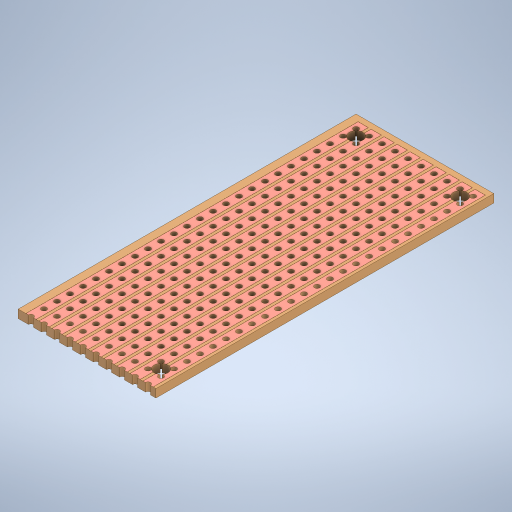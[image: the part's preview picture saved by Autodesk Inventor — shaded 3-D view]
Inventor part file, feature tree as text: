
AUTODESK INVENTOR PART (.ipt)
format: ipt  version: 2023 (Build 270158000, 158)  size: 1,360,384 bytes
history: mixed  units: in
note: dims shown in document units (in); Inventor stores cm internally (conversion verified against a paired STEP export)
features: sketch x10, extrude x9, projected_geometry x5, other x2, boolean_combine x1, imported_body x1
ambient origin geometry x8: Origin, YZ Plane, XZ Plane, XY Plane, X Axis, Y Axis, Z Axis, Center Point
bodies: Solid1 (imported_parasolid), Solid2 (imported_parasolid), Solid3 (imported_parasolid), Solid4 (imported_parasolid), Solid5 (imported_parasolid), Solid6 (imported_parasolid), Solid7 (imported_parasolid), Solid8 (imported_parasolid), Solid9 (imported_parasolid), Solid10 (imported_parasolid), Solid11 (imported_parasolid), Solid12 (imported_parasolid), Solid13 (imported_parasolid), Solid14 (imported_parasolid), Solid15 (imported_parasolid), Solid16 (imported_parasolid), Solid17 (imported_parasolid), Solid18 (imported_parasolid), Solid19 (imported_parasolid), Solid20 (imported_parasolid), Body2 (imported_parasolid), Body1 (imported_parasolid), Body3 (imported_parasolid), Body4 (imported_parasolid), Body5 (imported_parasolid), Body6 (imported_parasolid), Body7 (imported_parasolid), Body8 (imported_parasolid), Body9 (imported_parasolid), Body10 (imported_parasolid), Body11 (imported_parasolid), Body12 (imported_parasolid), Body13 (imported_parasolid), Body14 (imported_parasolid), Body15 (imported_parasolid), Body16 (imported_parasolid), Body17 (imported_parasolid), Body18 (imported_parasolid), Body19 (imported_parasolid), Body20 (imported_parasolid)
feature tree (28):
  other  "Repaired Geometry1"
  other  "Repaired Geometry2"
  sketch  "Sketch1"  dims[d0=0.1969in d1=0.0in d2=3.1063in d3=0.0in]
  extrude  "Extrusion1"  Depth=3.1063in TaperAngle=0.0deg
  sketch  "Sketch3"  dims[d8=0.4262in d9=0.0in d12=0.0512in d13=0.0in]
  extrude  "Extrusion2"  Depth=0.0512in TaperAngle=0.0deg
  extrude  "Extrusion3"  Depth=0.0512in TaperAngle=0.0deg
  extrude  "Extrusion4"  Depth=0.1043in
  sketch  "Sketch8"  dims[d25=0.3937in d26=0.0in d27=0.1043in]
  extrude  "Extrusion5"  Depth=0.1in
  boolean_combine  "Combine1"
  extrude  "Extrusion7"  Depth=0.1in
  extrude  "Extrusion8"  Depth=0.3937in
  extrude  "Extrusion9"  Depth=0.05in
  extrude  "Extrusion10"  Depth=2.3in
  sketch  "Sketch2"  dims[d4=0.0276in d5=0.0in d6=0.0512in d7=0.0in]
  sketch  "Sketch4"  dims[d14=0.0512in d15=0.0in d16=0.1043in]
  sketch  "Sketch6"  dims[d21=0.1in d22=0.05in]
  sketch  "Sketch7"  dims[d23=0.1in d24=0.05in]
  sketch  "Sketch9"  dims[d28=0.05in d29=0.05in]
  projected_geometry  "Projected Loop1"
  projected_geometry  "Projected Loop2"
  projected_geometry  "Projected Loop3"
  projected_geometry  "Projected Loop4"
  projected_geometry  "Projected Loop5"
  sketch  "Sketch10"  dims[d30=0.8in d31=2.3in]
  sketch  "Sketch11"  dims[d32=0.1043in d33=0.05in d34=0.1043in d35=0.8in d36=2.3in d37=0.5in d38=0.0in d39=0.05in d40=0.05in d10=0.0197in d11=1.9685in]
  imported_body  NMx_Import_Brep_tag  [imported B-rep: ~337 faces, bbox_mm=[26.9, 1.62, 66.0]]
